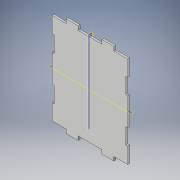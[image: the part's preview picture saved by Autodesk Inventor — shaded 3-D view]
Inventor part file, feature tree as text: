
AUTODESK INVENTOR PART (.ipt)
format: ipt  version: 2017 (Build 210142000, 142)  size: 161,792 bytes
history: native  units: in
note: dims shown in document units (in); Inventor stores cm internally (conversion verified against a paired STEP export)
features: extrude x3, sketch x3, plane x2, mirror x2, projected_geometry x2
ambient origin geometry x8: Origin, YZ Plane, XZ Plane, XY Plane, X Axis, Y Axis, Z Axis, Center Point
bodies: Solid1 (feature_tree)
feature tree (12):
  extrude  "Extrusion1"  Depth=46.0in
  extrude  "Extrusion2"  Depth=6.0in
  extrude  "Extrusion3"  Depth=2.0in TaperAngle=0.0deg
  plane  "Work Plane1"
  mirror  "Mirror1"
  plane  "Work Plane2"
  mirror  "Mirror2"
  sketch  "Sketch1"  dims[d0=38.0in d1=46.0in]
  sketch  "Sketch2"  dims[d2=1.0in d3=0.0in d4=6.0in]
  projected_geometry  "Projected Loop1"
  sketch  "Sketch3"  dims[d5=7.0in d6=2.0in d7=0.0in d8=8.0in d9=8.0in d10=1.0in d11=0.0in d12=14.0in d13=8.0in]
  projected_geometry  "Projected Loop2"
